FCSTD DOCUMENT  (FreeCAD 0.21R33771 (Git))
Label: tc2-sim-usb-pcb
License: All rights reserved
LicenseURL: http://en.wikipedia.org/wiki/All_rights_reserved
objects: Sketcher::SketchObject×1
note: 1 computed .brp shape members not serialized (recipe doc carries the construction recipe); baked Part::Feature solids carry a one-line shape summary decoded from their .brp

FEATURE [Sketcher::SketchObject] Sketch001  label="Boarder"
  FullyConstrained = true
  MapMode = 5
  sketch-geometry (23):
    g0: ArcOfCircle CenterX=2.7 CenterY=18 CenterZ=0 NormalX=0 NormalY=0 NormalZ=1 AngleXU=0 Radius=4.1 StartAngle=0.271168 EndAngle=3.14159
    g1: ArcOfCircle CenterX=2.7 CenterY=-32 CenterZ=0 NormalX=0 NormalY=0 NormalZ=1 AngleXU=0 Radius=4.1 StartAngle=3.14159 EndAngle=6.28319
    g2: LineSegment StartX=-1.4 StartY=-32 StartZ=0 EndX=-1.4 EndY=18 EndZ=0
    g3: LineSegment StartX=6.8 StartY=-8.5 StartZ=0 EndX=6.8 EndY=-32 EndZ=0
    g4: ArcOfCircle CenterX=8.3 CenterY=-8.5 CenterZ=0 NormalX=0 NormalY=0 NormalZ=1 AngleXU=0 Radius=1.5 StartAngle=1.5708 EndAngle=3.14159
    g5: LineSegment StartX=18.9 StartY=-5.5 StartZ=0 EndX=18.9 EndY=1.38 EndZ=0
    g6: LineSegment StartX=17.4 StartY=-7 StartZ=0 EndX=8.3 EndY=-7 EndZ=0
    g7: ArcOfCircle CenterX=17.4 CenterY=-5.5 CenterZ=0 NormalX=0 NormalY=0 NormalZ=1 AngleXU=0 Radius=1.5 StartAngle=4.71239 EndAngle=6.28319
    g8: ArcOfCircle CenterX=19.9 CenterY=1.38 CenterZ=0 NormalX=0 NormalY=0 NormalZ=1 AngleXU=0 Radius=1 StartAngle=1.5708 EndAngle=3.14159
    g9: LineSegment StartX=19.9 StartY=2.38 StartZ=0 EndX=20 EndY=2.38 EndZ=0
    g10: LineSegment StartX=21 StartY=17 StartZ=0 EndX=21 EndY=3.38 EndZ=0
    g11: ArcOfCircle CenterX=8.09537 CenterY=19.5 CenterZ=0 NormalX=0 NormalY=0 NormalZ=1 AngleXU=0 Radius=1.5 StartAngle=3.41276 EndAngle=4.71239
    g12: ArcOfCircle CenterX=20 CenterY=3.38 CenterZ=0 NormalX=0 NormalY=0 NormalZ=1 AngleXU=0 Radius=1 StartAngle=4.71239 EndAngle=6.28319
    g13: ArcOfCircle CenterX=20 CenterY=17 CenterZ=0 NormalX=0 NormalY=0 NormalZ=1 AngleXU=0 Radius=1 StartAngle=1.4e-15 EndAngle=1.5708
    g14: LineSegment StartX=8.09537 StartY=18 StartZ=0 EndX=9.64 EndY=18 EndZ=0
    g15: LineSegment StartX=11.137 StartY=17.33 StartZ=0 EndX=16.143 EndY=17.33 EndZ=0
    g16: LineSegment StartX=17.64 StartY=18 StartZ=0 EndX=20 EndY=18 EndZ=0
    g17: ArcOfCircle CenterX=9.64 CenterY=17 CenterZ=0 NormalX=0 NormalY=0 NormalZ=1 AngleXU=0 Radius=1 StartAngle=0.776342 EndAngle=1.5708
    g18: ArcOfCircle CenterX=17.64 CenterY=17 CenterZ=0 NormalX=0 NormalY=0 NormalZ=1 AngleXU=0 Radius=1 StartAngle=1.5708 EndAngle=2.36525
    g19: LineSegment StartX=10.3535 StartY=17.7007 StartZ=0 EndX=10.4235 EndY=17.6293 EndZ=0
    g20: ArcOfCircle CenterX=11.137 CenterY=18.33 CenterZ=0 NormalX=0 NormalY=0 NormalZ=1 AngleXU=0 Radius=1 StartAngle=3.91793 EndAngle=4.71239
    g21: LineSegment StartX=16.9265 StartY=17.7007 StartZ=0 EndX=16.8565 EndY=17.6293 EndZ=0
    g22: ArcOfCircle CenterX=16.143 CenterY=18.33 CenterZ=0 NormalX=0 NormalY=0 NormalZ=1 AngleXU=0 Radius=1 StartAngle=4.71239 EndAngle=5.50684
  constraints (58):
    c: Tangent(g1,g2) = 1.5708
    c: Tangent(g2,g0) = 1.5708
    c: Vertical(g2)
    c: Radius(g1) = 4.1
    c: DistanceY(g2,g2) = 50
    c: DistanceY(g-1,g0) = 18
    c: Vertical(g3)
    c: Tangent(g3,g4) = -1.5708
    c: Radius(g4) = 1.5
    c: Vertical(g5)
    c: Horizontal(g6)
    c: Tangent(g5,g7) = -1.5708
    c: Tangent(g6,g7) = 1.5708
    c: Equal(g7,g4)
    c: DistanceY(g6,g-1) = 7
    c: Tangent(g6,g4) = -1.5708
    c: DistanceX(g-1,g5) = 18.9
    c: DistanceX(g0,g-1) = 1.4
    c: DistanceX(g0) = 2.7
    c: Tangent(g1,g3) = 1.5708
    c: Tangent(g8,g5) = 1.5708
    c: Radius(g8) = 1
    c: Horizontal(g9)
    c: Tangent(g9,g8) = 1.5708
    c: Vertical(g10)
    c: DistanceY(g-1,g5) = 1.38
    c: Equal(g4,g11)
    c: Tangent(g11,g0) = 1.5708
    c: Tangent(g9,g12) = -1.5708
    c: Tangent(g10,g12) = 1.5708
    c: Radius(g12) = 1
    c: DistanceX(g-1,g10) = 21
    c: Tangent(g10,g13) = 1.5708
    c: Radius(g13) = 1
    c: Horizontal(g14)
    c: Horizontal(g15)
    c: Tangent(g14,g17) = 1.5708
    c: Tangent(g16,g18) = 1.5708
    c: Horizontal(g16)
    c: DistanceY(g15,g14) = 0.67
    c: Equal(g17,g18)
    c: Radius(g17) = 1
    c: Tangent(g16,g13) = 1.5708
    c: Horizontal(g16,g14)
    c: DistanceY(g-1,g11) = 18
    c: Tangent(g14,g11) = -1.5708
    c: DistanceX(g14,g16) = 8
    c: DistanceX(g0,g14) = 6.94
    c: Tangent(g20,g15) = -1.5708
    c: Tangent(g20,g19) = -1.5708
    c: Tangent(g19,g17) = 1.5708
    c: Equal(g20,g17)
    c: Distance(g19) = 0.1
    c: Tangent(g22,g15) = -1.5708
    c: Tangent(g22,g21) = 1.5708
    c: Tangent(g21,g18) = -1.5708
    c: Distance(g21) = 0.1
    c: Equal(g18,g22)
